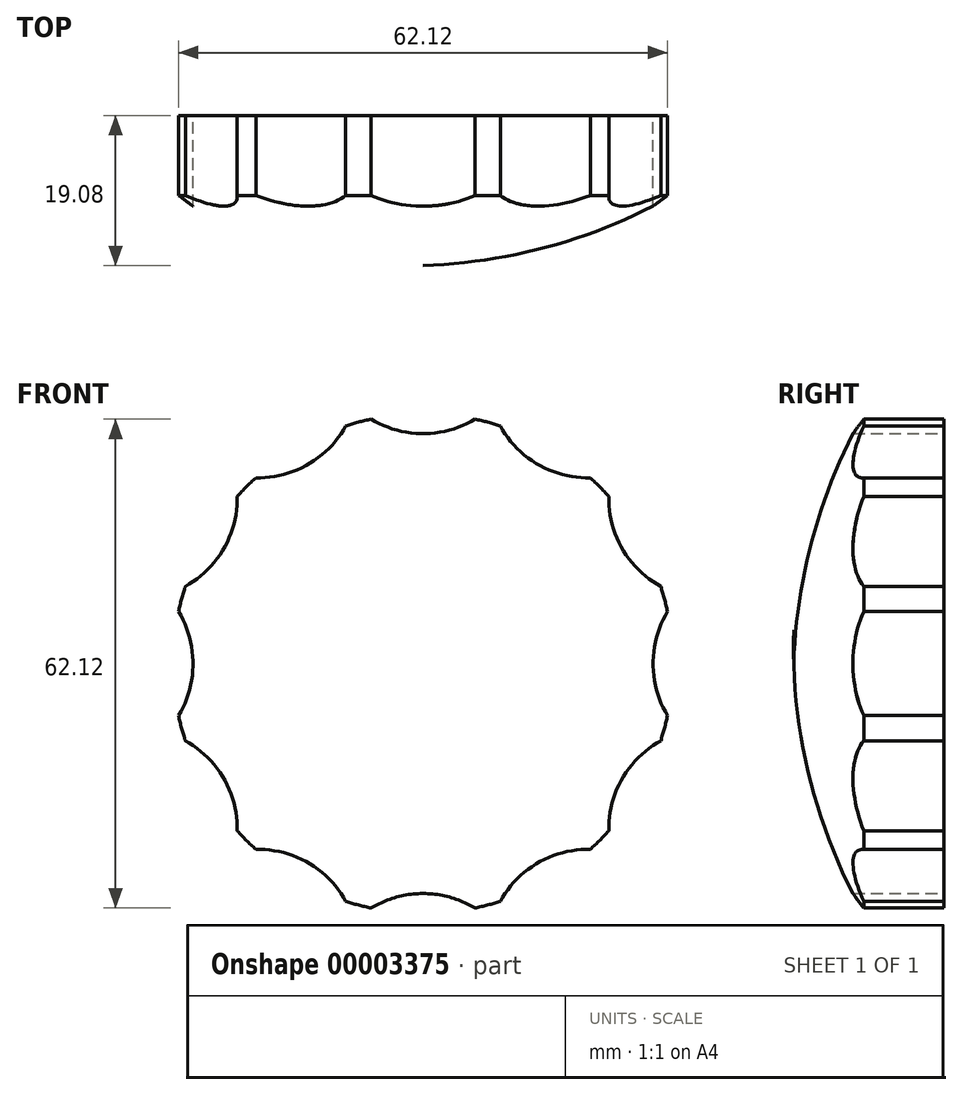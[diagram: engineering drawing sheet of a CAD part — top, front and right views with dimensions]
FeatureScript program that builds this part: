
annotation { "Feature Type Name" : "Feature", "Feature Type Description" : "" }
export const myFeature = defineFeature(function(context is Context, id is Id, definition is map)
    precondition{}
    {
        {
            var Q0;
            Q0=qCreatedBy(makeId("Right.planeOp"),FACE);
            var sketch = newSketch(context, id + "F0", { "sketchPlane" : qUnion([Q0])});
            skLineSegment(sketch, "E0.bottom", {"start": v(0, 0) * mm, "end": v(-19.05, 0) * mm});
            skLineSegment(sketch, "E0.top", {"start": v(0, 31.75) * mm, "end": v(-10.16, 31.75) * mm});
            skLineSegment(sketch, "E0.left", {"start": v(0, 0) * mm, "end": v(0, 31.75) * mm});
            skPoint(sketch, "E1.orphan", {"position": v(-5.53, 0) * mm});
            skArc(sketch, "E2", {"start": v(-10.16, 31.75) * mm, "mid": v(-16.53, 16.42) * mm, "end": v(-19.05, 0) * mm});
            skSolve(sketch);
        }
        {
            var Q0;
            Q0=makeQuery(id+"F0.imprint","IMPRINT",FACE,{"disambiguationData":[TD([[makeQuery(id+"F0.imprint","IMPRINT",EDGE,{"derivedFrom":sQuery(id+"F0.wireOp",EDGE,"E0.bottom")}),-1.0]])]});
            var Q1;
            Q1=sQuery(id+"F0.wireOp",EDGE,"E0.bottom");
            revolve(context, id + "F1", {"entities" : qUnion([Q0]), "axis" : qUnion([Q1]), "revolveType" : RevolveType.FULL});
        }
        {
            var Q0;
            Q0=qCreatedBy(makeId("Front.planeOp"),FACE);
            var sketch = newSketch(context, id + "F2", { "sketchPlane" : qUnion([Q0])});
            skCircle(sketch, "E3", {"center": v(-41.91, 0) * mm, "radius": 12.7 * mm});
            skCircle(sketch, "E4", {"center": v(0, 0) * mm, "radius": 41.91 * mm, "construction": true});
            skCircle(sketch, "E5", {"center": v(0, 0) * mm, "radius": 54.61 * mm, "construction": true});
            skCircle(sketch, "E6", {"center": v(0, 41.91) * mm, "radius": 12.7 * mm});
            skCircle(sketch, "E7", {"center": v(41.91, 0) * mm, "radius": 12.7 * mm});
            skCircle(sketch, "E8", {"center": v(0, -41.91) * mm, "radius": 12.7 * mm});
            skLineSegment(sketch, "E9", {"start": v(67.3, -38.86) * mm, "end": v(0, 0) * mm, "construction": true});
            skLineSegment(sketch, "E10", {"start": v(33.25, -57.58) * mm, "end": v(0, 0) * mm, "construction": true});
            skLineSegment(sketch, "E11", {"start": v(0, 0) * mm, "end": v(-107.5, 0) * mm});
            skCircle(sketch, "E12", {"center": v(-36.3, 20.95) * mm, "radius": 12.7 * mm});
            skCircle(sketch, "E13", {"center": v(-20.96, 36.3) * mm, "radius": 12.7 * mm});
            skCircle(sketch, "E14", {"center": v(20.96, -36.3) * mm, "radius": 12.7 * mm});
            skCircle(sketch, "E15", {"center": v(36.3, -20.95) * mm, "radius": 12.7 * mm});
            skLineSegment(sketch, "E16", {"start": v(39.45, 68.32) * mm, "end": v(0, 0) * mm, "construction": true});
            skLineSegment(sketch, "E17", {"start": v(71.1, 41.05) * mm, "end": v(0, 0) * mm, "construction": true});
            skCircle(sketch, "E18", {"center": v(-36.3, -20.96) * mm, "radius": 12.7 * mm});
            skCircle(sketch, "E19", {"center": v(-20.95, -36.3) * mm, "radius": 12.7 * mm});
            skCircle(sketch, "E20", {"center": v(20.95, 36.3) * mm, "radius": 12.7 * mm});
            skCircle(sketch, "E21", {"center": v(36.3, 20.96) * mm, "radius": 12.7 * mm});
            skSolve(sketch);
        }
        {
            var Q0;
            Q0 = qSketchRegion(id + "F2", true);
            extrude(context, id + "F3", {"entities" : qUnion([Q0]), "operationType" : NewBodyOperationType.REMOVE, "depth" : 38.1 * mm});
        }
    });
